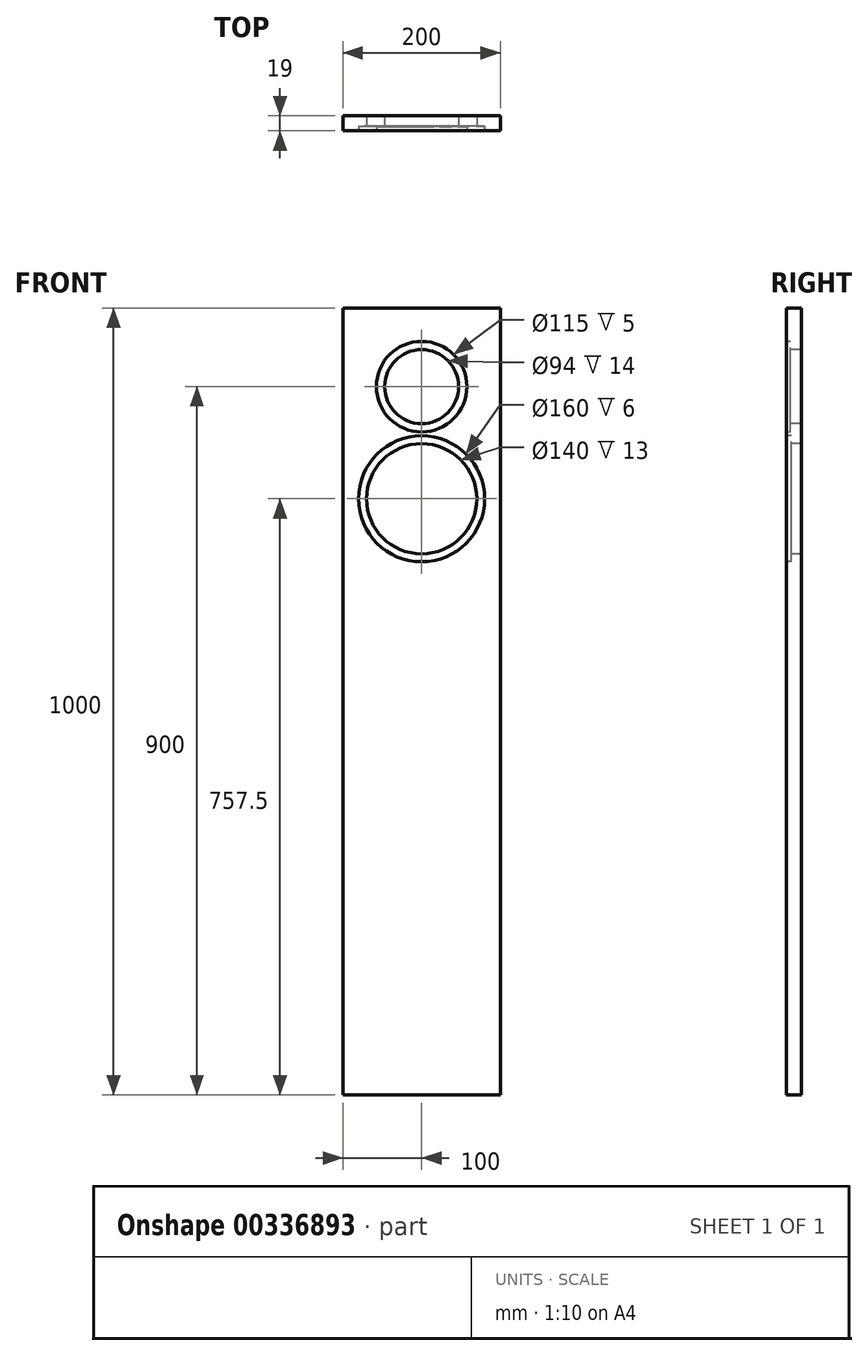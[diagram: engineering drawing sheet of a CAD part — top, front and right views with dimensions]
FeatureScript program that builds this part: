
annotation { "Feature Type Name" : "Feature", "Feature Type Description" : "" }
export const myFeature = defineFeature(function(context is Context, id is Id, definition is map)
    precondition{}
    {
        {
            var Q0;
            Q0=qCreatedBy(makeId("Front.planeOp"),FACE);
            var sketch = newSketch(context, id + "F0", { "sketchPlane" : qUnion([Q0])});
            skLineSegment(sketch, "E0.bottom", {"start": v(-100, 500) * mm, "end": v(100, 500) * mm});
            skLineSegment(sketch, "E0.top", {"start": v(-100, -500) * mm, "end": v(100, -500) * mm});
            skLineSegment(sketch, "E0.left", {"start": v(-100, 500) * mm, "end": v(-100, -500) * mm});
            skLineSegment(sketch, "E0.right", {"start": v(100, 500) * mm, "end": v(100, -500) * mm});
            skPoint(sketch, "E0.middle", {"position": v(0, 0) * mm});
            skSolve(sketch);
        }
        {
            var Q0;
            Q0=makeQuery(id+"F0.imprint","IMPRINT",FACE,{"disambiguationData":[TD([[makeQuery(id+"F0.imprint","IMPRINT",EDGE,{"derivedFrom":sQuery(id+"F0.wireOp",EDGE,"E0.bottom")}),-1.0]])]});
            var Q1;
            Q1 = qSketchRegion(id + "FpgMxrdpVEIP0U4_1", true);
            extrude(context, id + "F1", {"entities" : qUnion([Q0, Q1]), "depth" : 19 * mm});
        }
        {
            var Q0;
            Q0=makeQuery(id+"F1.opExtrude","CAP_FACE",FACE,{"disambiguationData":[OSD([sQuery(id+"F0.wireOp",EDGE,"E0.bottom"),sQuery(id+"F0.wireOp",EDGE,"E0.top"),sQuery(id+"F0.wireOp",EDGE,"E0.left"),sQuery(id+"F0.wireOp",EDGE,"E0.right")])],"isStart":false});
            var sketch = newSketch(context, id + "F2", { "sketchPlane" : qUnion([Q0])});
            skCircle(sketch, "E1", {"center": v(0, 400) * mm, "radius": 57.5 * mm});
            skSolve(sketch);
        }
        {
            var Q0;
            Q0 = qSketchRegion(id + "F2", true);
            extrude(context, id + "F3", {"entities" : qUnion([Q0]), "operationType" : NewBodyOperationType.REMOVE, "depth" : -5 * mm});
        }
        {
            var Q0;
            Q0=makeQuery(id+"F2.imprint","IMPRINT",FACE,{"disambiguationData":[TD([[makeQuery(id+"F2.imprint","IMPRINT",EDGE,{"derivedFrom":sQuery(id+"F2.wireOp",EDGE,"E1")}),1.0]])]});
            var sketch = newSketch(context, id + "F4", { "sketchPlane" : qUnion([Q0])});
            skCircle(sketch, "E2", {"center": v(0, 400) * mm, "radius": 47 * mm});
            skSolve(sketch);
        }
        {
            var Q0;
            Q0 = qSketchRegion(id + "F4", true);
            extrude(context, id + "F5", {"entities" : qUnion([Q0]), "operationType" : NewBodyOperationType.REMOVE, "oppositeDirection" : true, "depth" : 25 * mm});
        }
        {
            var Q0;
            Q0=makeQuery(id+"F2.imprint","IMPRINT",FACE,{"disambiguationData":[TD([[makeQuery(id+"F2.imprint","IMPRINT",EDGE,{"derivedFrom":sQuery(id+"F2.wireOp",EDGE,"E1")}),-1.0]])]});
            var sketch = newSketch(context, id + "F6", { "sketchPlane" : qUnion([Q0])});
            skCircle(sketch, "E3", {"center": v(0, 257.5) * mm, "radius": 80 * mm});
            skSolve(sketch);
        }
        {
            var Q0;
            Q0 = qSketchRegion(id + "F6", true);
            extrude(context, id + "F7", {"entities" : qUnion([Q0]), "operationType" : NewBodyOperationType.REMOVE, "oppositeDirection" : true, "depth" : 6 * mm});
        }
        {
            var Q0;
            Q0=makeQuery(id+"F2.imprint","IMPRINT",FACE,{"disambiguationData":[TD([[makeQuery(id+"F2.imprint","IMPRINT",EDGE,{"derivedFrom":sQuery(id+"F2.wireOp",EDGE,"E1")}),-1.0]])]});
            var sketch = newSketch(context, id + "F8", { "sketchPlane" : qUnion([Q0])});
            skCircle(sketch, "E4", {"center": v(0, 257.5) * mm, "radius": 70 * mm});
            skSolve(sketch);
        }
        {
            var Q0;
            Q0 = qSketchRegion(id + "F8", true);
            var Q1;
            Q1=makeQuery(id+"F0.imprint","IMPRINT",FACE,{"disambiguationData":[TD([[makeQuery(id+"F0.imprint","IMPRINT",EDGE,{"derivedFrom":sQuery(id+"F0.wireOp",EDGE,"E0.bottom")}),-1.0]])]});
            extrude(context, id + "F9", {"entities" : qUnion([Q0, Q1]), "operationType" : NewBodyOperationType.REMOVE, "oppositeDirection" : true, "depth" : 25 * mm});
        }
    });
